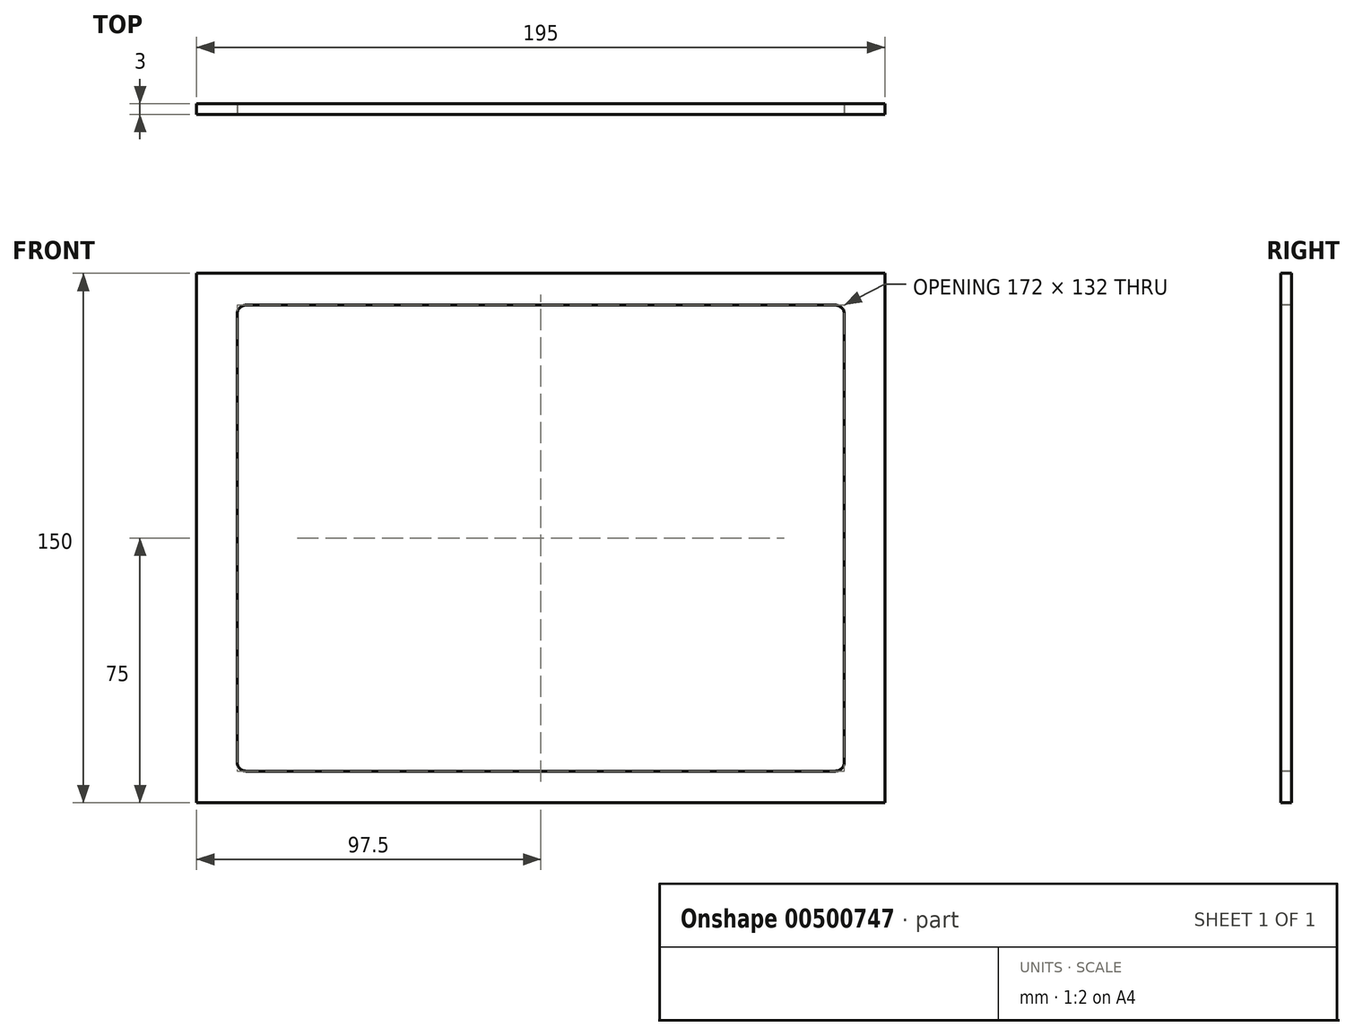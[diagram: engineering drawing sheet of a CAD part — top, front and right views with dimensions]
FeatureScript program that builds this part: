
annotation { "Feature Type Name" : "Feature", "Feature Type Description" : "" }
export const myFeature = defineFeature(function(context is Context, id is Id, definition is map)
    precondition{}
    {
        {
            var Q0;
            Q0=qCreatedBy(makeId("Front.planeOp"),FACE);
            var sketch = newSketch(context, id + "F0", { "sketchPlane" : qUnion([Q0])});
            skLineSegment(sketch, "E0.bottom", {"start": v(-86, 66) * mm, "end": v(86, 66) * mm});
            skLineSegment(sketch, "E0.top", {"start": v(-86, -66) * mm, "end": v(86, -66) * mm});
            skLineSegment(sketch, "E0.left", {"start": v(-86, 66) * mm, "end": v(-86, -66) * mm});
            skLineSegment(sketch, "E0.right", {"start": v(86, 66) * mm, "end": v(86, -66) * mm});
            skLineSegment(sketch, "E1.bottom", {"start": v(-97.5, 75) * mm, "end": v(97.5, 75) * mm});
            skLineSegment(sketch, "E1.top", {"start": v(-97.5, -75) * mm, "end": v(97.5, -75) * mm});
            skLineSegment(sketch, "E1.left", {"start": v(-97.5, 75) * mm, "end": v(-97.5, -75) * mm});
            skLineSegment(sketch, "E1.right", {"start": v(97.5, 75) * mm, "end": v(97.5, -75) * mm});
            skSolve(sketch);
        }
        {
            var Q0;
            Q0 = qSketchRegion(id + "F0", true);
            extrude(context, id + "F1", {"entities" : qUnion([Q0]), "oppositeDirection" : true, "depth" : 3 * mm, "offsetDistance" : 25 * mm});
        }
        {
            var Q0;
            Q0=makeQuery(id+"F1.opExtrude","SWEPT_EDGE",EDGE,{"disambiguationData":[OSD([sQuery(id+"F0.wireOp",EDGE,"E0.top"),sQuery(id+"F0.wireOp",EDGE,"E0.left")])]});
            var Q1;
            Q1=makeQuery(id+"F1.opExtrude","SWEPT_EDGE",EDGE,{"disambiguationData":[OSD([sQuery(id+"F0.wireOp",EDGE,"E0.top"),sQuery(id+"F0.wireOp",EDGE,"E0.right")])]});
            var Q2;
            Q2=makeQuery(id+"F1.opExtrude","SWEPT_EDGE",EDGE,{"disambiguationData":[OSD([sQuery(id+"F0.wireOp",EDGE,"E0.bottom"),sQuery(id+"F0.wireOp",EDGE,"E0.right")])]});
            var Q3;
            Q3=makeQuery(id+"F1.opExtrude","SWEPT_EDGE",EDGE,{"disambiguationData":[OSD([sQuery(id+"F0.wireOp",EDGE,"E0.bottom"),sQuery(id+"F0.wireOp",EDGE,"E0.left")])]});
            fillet(context, id + "F2", {"entities" : qUnion([Q0, Q1, Q2, Q3]), "radius" : 2.5 * mm, "tangentPropagation" : true, "allowEdgeOverflow" : false});
        }
    });
